# Revit family: Plumbing-Soap-Dispensers-Sloan-Valve-ESD-500
name_source: partatom
category: Specialty Equipment
units: mm (PartAtom-declared; Revit-internal decimal feet)

## family parameters
Cut with Voids When Loaded = No
Host = Face
OmniClass Number = 23.40.20.21.34
OmniClass Title = Soap Holders, Dispensers
Part Type = Normal
Room Calculation Point = No
Round Connector Dimension = Use Diameter
Shared = No

## types (5) — shared parameters
Apparent Load = 750 VA
Assembly Code = D2010
Current = 15 A
Default Elevation = 0"
Depth = 5 1/4"
Edition number = 1
Height = 5"
Keynote = 15410
Manufacturer = Sloan Valve
Number of Poles = 3
Power Factor = 0.8
Product data url = https://bimobject.com
URL = www.sloanvalve.com
Voltage = 120 V
Width = 2"

## per-type parameters (varying)
| type | Description | Part Number | Product Material |
| ESD-500-BN | Brushed Nickel Finish, Sloan® Deck-Mounted Foam Soap Dispenser. | 3346138 | Sloan Valve - Finish - Brushed Nickel |
| ESD-500-CP | Polished Chrome Finish, Sloan® Deck-Mounted Foam Soap Dispenser. | 3346087 | Sloan Valve - Finish - Polished Chrome |
| ESD-500-GR | Graphite Finish, Sloan® Deck-Mounted Foam Soap Dispenser. | 3346154 | Sloan Valve - Finish - Graphite |
| ESD-500-PB | Polished Brass Finish, Sloan® Deck-Mounted Foam Soap Dispenser. | 3346144 | Sloan Valve - Finish - Polished Brass |
| ESD-500-SF | Brushed Stainless Finish, Sloan® Deck-Mounted Foam Soap
Dispenser | 3346141 | Sloan Valve - Stainless Steel - Brushed |

note: column(s) folded — value = type name in every type: Model

## geometry (parser evidence)
native form markers: Sweep x3
no freeform markers — native parametric forms only
